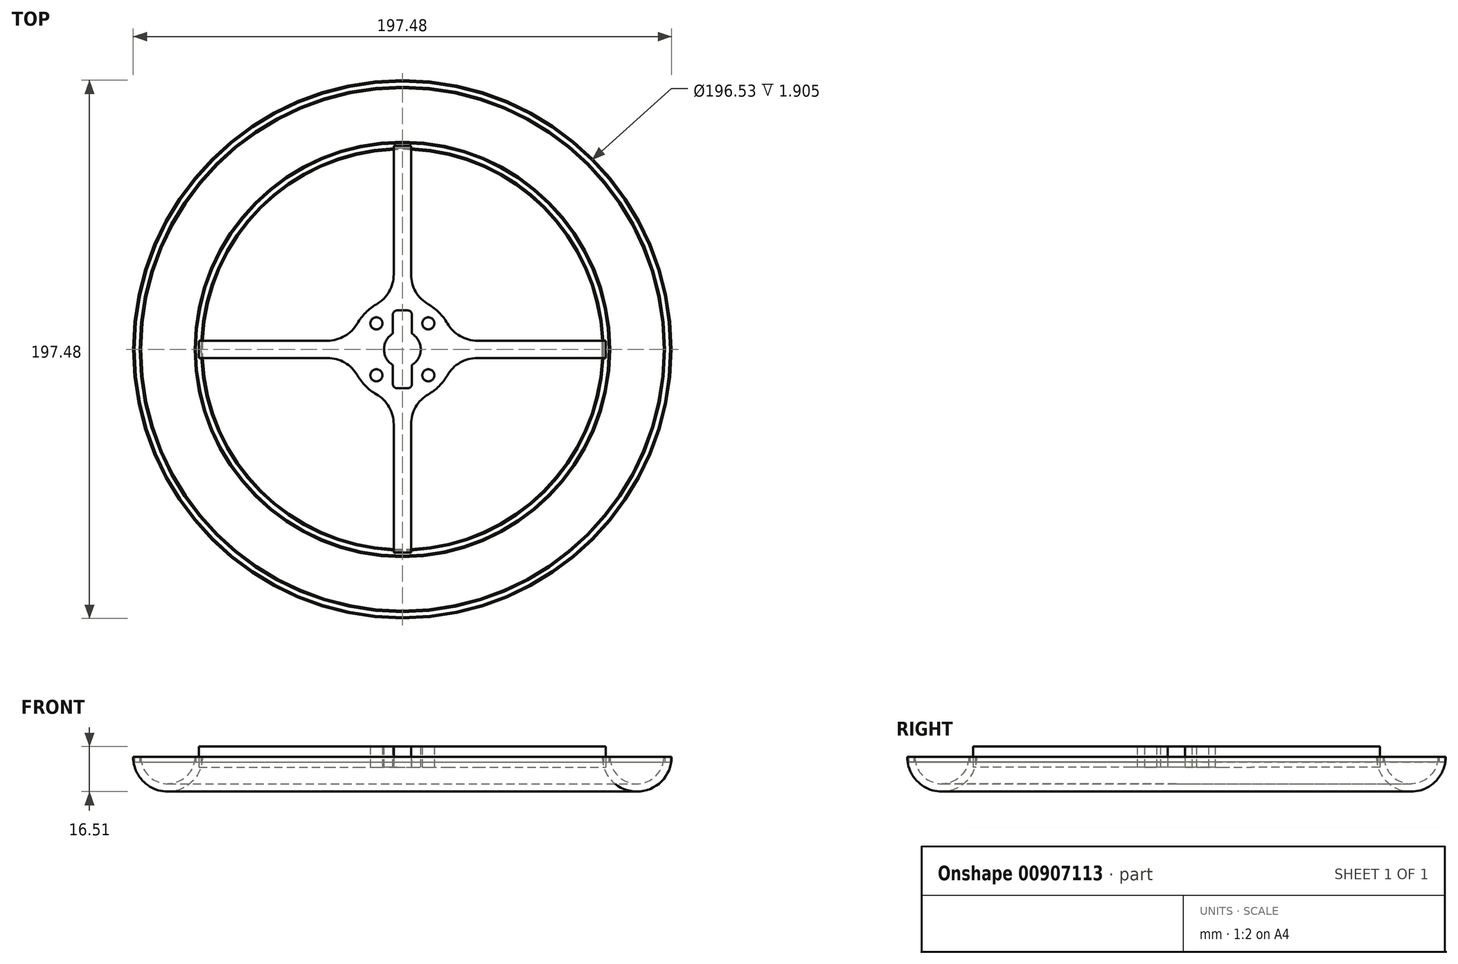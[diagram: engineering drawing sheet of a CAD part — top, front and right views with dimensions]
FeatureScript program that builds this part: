
annotation { "Feature Type Name" : "Feature", "Feature Type Description" : "" }
export const myFeature = defineFeature(function(context is Context, id is Id, definition is map)
    precondition{}
    {
        {
            var Q0;
            Q0=qCreatedBy(makeId("Front.planeOp"),FACE);
            var sketch = newSketch(context, id + "F0", { "sketchPlane" : qUnion([Q0])});
            skLineSegment(sketch, "E0", {"start": v(0, 25.4) * mm, "end": v(0, -25.4) * mm, "construction": true});
            skArc(sketch, "E1", {"start": v(-95.89, 0) * mm, "mid": v(-86.04, -9.84) * mm, "end": v(-76.2, 0) * mm});
            skArc(sketch, "E2", {"start": v(-98.74, 0) * mm, "mid": v(-86.04, -12.7) * mm, "end": v(-73.34, 0) * mm});
            skLineSegment(sketch, "E3", {"start": v(-98.74, 0) * mm, "end": v(-95.89, 0) * mm});
            skLineSegment(sketch, "E4.trimOffspring", {"start": v(-76.2, 0) * mm, "end": v(-73.34, 0) * mm});
            skSolve(sketch);
        }
        {
            var Q0;
            Q0=makeQuery(id+"F0.imprint","IMPRINT",FACE,{"disambiguationData":[TD([[makeQuery(id+"F0.imprint","IMPRINT",EDGE,{"derivedFrom":sQuery(id+"F0.wireOp",EDGE,"E1")}),1.0]])]});
            var Q1;
            Q1=makeQuery(id+"F0.imprint","IMPRINT",FACE,{"disambiguationData":[TD([[makeQuery(id+"F0.imprint","IMPRINT",EDGE,{"derivedFrom":sQuery(id+"F0.wireOp",EDGE,"E1")}),-1.0]])]});
            var Q2;
            Q2=sQuery(id+"F0.wireOp",EDGE,"E0");
            revolve(context, id + "F1", {"surfaceOperationType" : NewSurfaceOperationType.NEW, "entities" : qUnion([Q0, Q1]), "axis" : qUnion([Q2]), "revolveType" : RevolveType.FULL});
        }
        {
            var Q0;
            Q0=qCreatedBy(makeId("Front.planeOp"),FACE);
            var sketch = newSketch(context, id + "F2", { "sketchPlane" : qUnion([Q0])});
            skLineSegment(sketch, "E5.bottom", {"start": v(-98.27, 0) * mm, "end": v(-96.36, 0) * mm});
            skLineSegment(sketch, "E5.top", {"start": v(-98.27, -1.9) * mm, "end": v(-96.36, -1.9) * mm});
            skLineSegment(sketch, "E5.left", {"start": v(-98.27, 0) * mm, "end": v(-98.27, -1.9) * mm});
            skLineSegment(sketch, "E5.right", {"start": v(-96.36, 0) * mm, "end": v(-96.36, -1.9) * mm});
            skLineSegment(sketch, "E6.bottom", {"start": v(-75.72, 0) * mm, "end": v(-73.82, 0) * mm});
            skLineSegment(sketch, "E6.top", {"start": v(-75.72, -1.9) * mm, "end": v(-73.82, -1.9) * mm});
            skLineSegment(sketch, "E6.left", {"start": v(-75.72, 0) * mm, "end": v(-75.72, -1.9) * mm});
            skLineSegment(sketch, "E6.right", {"start": v(-73.82, 0) * mm, "end": v(-73.82, -1.9) * mm});
            skLineSegment(sketch, "E7", {"start": v(-97.31, 0) * mm, "end": v(-97.31, -1.9) * mm, "construction": true});
            skLineSegment(sketch, "E8", {"start": v(-98.27, -0.95) * mm, "end": v(-96.36, -0.95) * mm, "construction": true});
            skLineSegment(sketch, "E9", {"start": v(-74.77, 0) * mm, "end": v(-74.77, -1.9) * mm, "construction": true});
            skLineSegment(sketch, "E10", {"start": v(-75.72, -0.95) * mm, "end": v(-73.82, -0.95) * mm, "construction": true});
            skSolve(sketch);
        }
        {
            var Q0;
            Q0 = qSketchRegion(id + "F2", true);
            var Q1;
            Q1=sQuery(id+"F0.wireOp",EDGE,"E0");
            revolve(context, id + "F3", {"operationType" : NewBodyOperationType.REMOVE, "surfaceOperationType" : NewSurfaceOperationType.NEW, "entities" : qUnion([Q0]), "axis" : qUnion([Q1]), "revolveType" : RevolveType.FULL, "oppositeDirection" : true});
        }
        {
            var Q0;
            Q0=makeQuery(id+"F3.boolean.opBoolean","SPLIT",FACE,{"disambiguationData":[TD([makeQuery(id+"F1.opRevolve","SWEPT_FACE",FACE,{"disambiguationData":[OSD([sQuery(id+"F0.wireOp",EDGE,"E2")])]})])],"derivedFrom":makeQuery(id+"F1.opRevolve","SWEPT_FACE",FACE,{"disambiguationData":[OSD([sQuery(id+"F0.wireOp",EDGE,"E4.trimOffspring")])]})});
            var sketch = newSketch(context, id + "F4", { "sketchPlane" : qUnion([Q0])});
            skLineSegment(sketch, "E11.bottom", {"start": v(-50.8, 3.18) * mm, "end": v(50.8, 3.18) * mm});
            skLineSegment(sketch, "E11.top", {"start": v(-50.8, -3.17) * mm, "end": v(50.8, -3.17) * mm});
            skLineSegment(sketch, "E11.left", {"start": v(-50.8, 3.17) * mm, "end": v(-50.8, -3.17) * mm});
            skLineSegment(sketch, "E11.right", {"start": v(50.8, 3.17) * mm, "end": v(50.8, -3.17) * mm});
            skLineSegment(sketch, "E12.bottom", {"start": v(3.17, 50.8) * mm, "end": v(-3.17, 50.8) * mm});
            skLineSegment(sketch, "E12.top", {"start": v(3.17, -50.8) * mm, "end": v(-3.17, -50.8) * mm});
            skLineSegment(sketch, "E12.left", {"start": v(3.18, 50.8) * mm, "end": v(3.18, -50.8) * mm});
            skLineSegment(sketch, "E12.right", {"start": v(-3.17, 50.8) * mm, "end": v(-3.17, -50.8) * mm});
            skLineSegment(sketch, "E13", {"start": v(0, 50.8) * mm, "end": v(0, -50.8) * mm, "construction": true});
            skLineSegment(sketch, "E14", {"start": v(-3.18, 0) * mm, "end": v(3.17, 0) * mm, "construction": true});
            skLineSegment(sketch, "E15", {"start": v(-50.8, 0) * mm, "end": v(50.8, 0) * mm, "construction": true});
            skLineSegment(sketch, "E16", {"start": v(0, 3.17) * mm, "end": v(0, -3.17) * mm, "construction": true});
            skSolve(sketch);
        }
        {
            var Q0;
            {var subQ0=sQuery(id+"F4.wireOp",EDGE,"E11.left");Q0=makeQuery(id+"F4.imprint","IMPRINT",FACE,{"disambiguationData":[TD([[makeQuery(id+"F4.imprint","IMPRINT",EDGE,{"derivedFrom":subQ0}),1.0]])]});}
            var Q1;
            {var subQ0=sQuery(id+"F4.wireOp",EDGE,"E11.right");Q1=makeQuery(id+"F4.imprint","IMPRINT",FACE,{"disambiguationData":[TD([[makeQuery(id+"F4.imprint","IMPRINT",EDGE,{"derivedFrom":subQ0}),-1.0]])]});}
            var Q2;
            {var subQ5=sQuery(id+"F4.wireOp",EDGE,"E12.bottom");Q2=makeQuery(id+"F4.imprint","IMPRINT",FACE,{"disambiguationData":[TD([[makeQuery(id+"F4.imprint","IMPRINT",EDGE,{"derivedFrom":subQ5}),1.0]])]});}
            var Q3;
            {var subQ5=sQuery(id+"F4.wireOp",EDGE,"E12.top");Q3=makeQuery(id+"F4.imprint","IMPRINT",FACE,{"disambiguationData":[TD([[makeQuery(id+"F4.imprint","IMPRINT",EDGE,{"derivedFrom":subQ5}),-1.0]])]});}
            var Q4;
            {var subQ0=sQuery(id+"F4.wireOp",EDGE,"E12.right");var subQ1=sQuery(id+"F4.wireOp",EDGE,"E11.bottom");var subQ2=makeQuery(id+"F4.imprint","INTERSECT",VERTEX,{"derivedFrom":[subQ1,subQ0]});Q4=makeQuery(id+"F4.imprint","IMPRINT",FACE,{"disambiguationData":[TD([[makeQuery(id+"F4.imprint","IMPRINT",EDGE,{"disambiguationData":[TD([[subQ2,-1.0]])],"derivedFrom":subQ1}),-1.0]])]});}
            extrude(context, id + "F5", {"entities" : qUnion([Q0, Q1, Q2, Q3, Q4]), "depth" : 25.4 * mm, "offsetDistance" : 25.4 * mm});
        }
        {
            var Q0;
            Q0=makeQuery(id+"F5.opExtrude","SWEPT_BODY",BODY,{"disambiguationData":[OSD([sQuery(id+"F4.wireOp",EDGE,"E11.bottom"),sQuery(id+"F4.wireOp",EDGE,"E11.top"),sQuery(id+"F4.wireOp",EDGE,"E11.left"),sQuery(id+"F4.wireOp",EDGE,"E11.right"),sQuery(id+"F4.wireOp",EDGE,"E12.bottom"),sQuery(id+"F4.wireOp",EDGE,"E12.top"),sQuery(id+"F4.wireOp",EDGE,"E12.left"),sQuery(id+"F4.wireOp",EDGE,"E12.right")])]});
            deleteBodies(context, id + "F6", {"entities" : qUnion([Q0])});
        }
        {
            var Q0;
            Q0=qCreatedBy(makeId("Top.planeOp"),FACE);
            var sketch = newSketch(context, id + "F7", { "sketchPlane" : qUnion([Q0])});
            skLineSegment(sketch, "E17.bottom", {"start": v(-74.61, 3.17) * mm, "end": v(74.61, 3.17) * mm});
            skLineSegment(sketch, "E17.top", {"start": v(-74.61, -3.18) * mm, "end": v(74.61, -3.18) * mm});
            skLineSegment(sketch, "E17.left", {"start": v(74.61, 3.18) * mm, "end": v(74.61, -3.17) * mm});
            skLineSegment(sketch, "E17.right", {"start": v(-74.61, 3.18) * mm, "end": v(-74.61, -3.18) * mm});
            skLineSegment(sketch, "E18", {"start": v(74.61, 0) * mm, "end": v(-74.61, 0) * mm, "construction": true});
            skLineSegment(sketch, "E19", {"start": v(0, 3.17) * mm, "end": v(0, -3.17) * mm, "construction": true});
            skLineSegment(sketch, "E20.bottom", {"start": v(-3.18, 74.61) * mm, "end": v(3.18, 74.61) * mm});
            skLineSegment(sketch, "E20.top", {"start": v(-3.18, -74.61) * mm, "end": v(3.18, -74.61) * mm});
            skLineSegment(sketch, "E20.left", {"start": v(-3.18, 74.61) * mm, "end": v(-3.18, -74.61) * mm});
            skLineSegment(sketch, "E20.right", {"start": v(3.17, 74.61) * mm, "end": v(3.17, -74.61) * mm});
            skLineSegment(sketch, "E21", {"start": v(0, 74.61) * mm, "end": v(0, -74.61) * mm, "construction": true});
            skLineSegment(sketch, "E22", {"start": v(-3.17, 0) * mm, "end": v(3.17, 0) * mm, "construction": true});
            skCircle(sketch, "E23", {"center": v(0, 0) * mm, "radius": 19.05 * mm});
            skSolve(sketch);
        }
        {
            var Q0;
            {var subQ0=sQuery(id+"F7.wireOp",EDGE,"E17.right");Q0=makeQuery(id+"F7.imprint","IMPRINT",FACE,{"disambiguationData":[TD([[makeQuery(id+"F7.imprint","IMPRINT",EDGE,{"derivedFrom":subQ0}),1.0]])]});}
            var Q1;
            {var subQ0=sQuery(id+"F7.wireOp",EDGE,"E17.left");Q1=makeQuery(id+"F7.imprint","IMPRINT",FACE,{"disambiguationData":[TD([[makeQuery(id+"F7.imprint","IMPRINT",EDGE,{"derivedFrom":subQ0}),-1.0]])]});}
            var Q2;
            {var subQ5=sQuery(id+"F7.wireOp",EDGE,"E20.bottom");Q2=makeQuery(id+"F7.imprint","IMPRINT",FACE,{"disambiguationData":[TD([[makeQuery(id+"F7.imprint","IMPRINT",EDGE,{"derivedFrom":subQ5}),-1.0]])]});}
            var Q3;
            {var subQ5=sQuery(id+"F7.wireOp",EDGE,"E20.top");Q3=makeQuery(id+"F7.imprint","IMPRINT",FACE,{"disambiguationData":[TD([[makeQuery(id+"F7.imprint","IMPRINT",EDGE,{"derivedFrom":subQ5}),1.0]])]});}
            var Q4;
            {var subQ0=sQuery(id+"F7.wireOp",EDGE,"E20.left");var subQ1=sQuery(id+"F7.wireOp",EDGE,"E17.bottom");var subQ2=makeQuery(id+"F7.imprint","INTERSECT",VERTEX,{"derivedFrom":[subQ1,subQ0]});Q4=makeQuery(id+"F7.imprint","IMPRINT",FACE,{"disambiguationData":[TD([[makeQuery(id+"F7.imprint","IMPRINT",EDGE,{"disambiguationData":[TD([[subQ2,-1.0]])],"derivedFrom":subQ1}),-1.0]])]});}
            var Q5;
            {var subQ0=sQuery(id+"F7.wireOp",EDGE,"E23");var subQ1=sQuery(id+"F7.wireOp",EDGE,"E17.bottom");var subQ2=makeQuery(id+"F7.imprint","INTERSECT",VERTEX,{"disambiguationData":[OD(0.0)],"derivedFrom":[subQ1,subQ0]});Q5=makeQuery(id+"F7.imprint","IMPRINT",FACE,{"disambiguationData":[TD([[makeQuery(id+"F7.imprint","IMPRINT",EDGE,{"disambiguationData":[TD([[subQ2,-1.0]])],"derivedFrom":subQ1}),-1.0]])]});}
            var Q6;
            {var subQ0=sQuery(id+"F7.wireOp",EDGE,"E23");var subQ1=sQuery(id+"F7.wireOp",EDGE,"E17.bottom");var subQ2=makeQuery(id+"F7.imprint","INTERSECT",VERTEX,{"disambiguationData":[OD(1.0)],"derivedFrom":[subQ1,subQ0]});Q6=makeQuery(id+"F7.imprint","IMPRINT",FACE,{"disambiguationData":[TD([[makeQuery(id+"F7.imprint","IMPRINT",EDGE,{"disambiguationData":[TD([[subQ2,1.0]])],"derivedFrom":subQ1}),-1.0]])]});}
            var Q7;
            {var subQ0=sQuery(id+"F7.wireOp",EDGE,"E20.left");var subQ1=sQuery(id+"F7.wireOp",EDGE,"E17.top");var subQ2=makeQuery(id+"F7.imprint","INTERSECT",VERTEX,{"derivedFrom":[subQ1,subQ0]});Q7=makeQuery(id+"F7.imprint","IMPRINT",FACE,{"disambiguationData":[TD([[makeQuery(id+"F7.imprint","IMPRINT",EDGE,{"disambiguationData":[TD([[subQ2,-1.0]])],"derivedFrom":subQ1}),-1.0]])]});}
            var Q8;
            {var subQ0=sQuery(id+"F7.wireOp",EDGE,"E20.left");var subQ1=sQuery(id+"F7.wireOp",EDGE,"E17.bottom");var subQ2=makeQuery(id+"F7.imprint","INTERSECT",VERTEX,{"derivedFrom":[subQ1,subQ0]});Q8=makeQuery(id+"F7.imprint","IMPRINT",FACE,{"disambiguationData":[TD([[makeQuery(id+"F7.imprint","IMPRINT",EDGE,{"disambiguationData":[TD([[subQ2,-1.0]])],"derivedFrom":subQ1}),1.0]])]});}
            var Q9;
            {var subQ0=sQuery(id+"F7.wireOp",EDGE,"E23");var subQ1=sQuery(id+"F7.wireOp",EDGE,"E17.bottom");var subQ2=makeQuery(id+"F7.imprint","INTERSECT",VERTEX,{"disambiguationData":[OD(1.0)],"derivedFrom":[subQ1,subQ0]});Q9=makeQuery(id+"F7.imprint","IMPRINT",FACE,{"disambiguationData":[TD([[makeQuery(id+"F7.imprint","IMPRINT",EDGE,{"disambiguationData":[TD([[subQ2,1.0]])],"derivedFrom":subQ1}),1.0]])]});}
            var Q10;
            {var subQ0=sQuery(id+"F7.wireOp",EDGE,"E23");var subQ1=sQuery(id+"F7.wireOp",EDGE,"E17.bottom");var subQ2=makeQuery(id+"F7.imprint","INTERSECT",VERTEX,{"disambiguationData":[OD(0.0)],"derivedFrom":[subQ1,subQ0]});Q10=makeQuery(id+"F7.imprint","IMPRINT",FACE,{"disambiguationData":[TD([[makeQuery(id+"F7.imprint","IMPRINT",EDGE,{"disambiguationData":[TD([[subQ2,-1.0]])],"derivedFrom":subQ1}),1.0]])]});}
            var Q11;
            {var subQ0=sQuery(id+"F7.wireOp",EDGE,"E23");var subQ1=sQuery(id+"F7.wireOp",EDGE,"E17.top");var subQ2=makeQuery(id+"F7.imprint","INTERSECT",VERTEX,{"disambiguationData":[OD(0.0)],"derivedFrom":[subQ1,subQ0]});Q11=makeQuery(id+"F7.imprint","IMPRINT",FACE,{"disambiguationData":[TD([[makeQuery(id+"F7.imprint","IMPRINT",EDGE,{"disambiguationData":[TD([[subQ2,-1.0]])],"derivedFrom":subQ1}),-1.0]])]});}
            var Q12;
            {var subQ0=sQuery(id+"F7.wireOp",EDGE,"E23");var subQ1=sQuery(id+"F7.wireOp",EDGE,"E17.top");var subQ2=makeQuery(id+"F7.imprint","INTERSECT",VERTEX,{"disambiguationData":[OD(1.0)],"derivedFrom":[subQ1,subQ0]});Q12=makeQuery(id+"F7.imprint","IMPRINT",FACE,{"disambiguationData":[TD([[makeQuery(id+"F7.imprint","IMPRINT",EDGE,{"disambiguationData":[TD([[subQ2,1.0]])],"derivedFrom":subQ1}),-1.0]])]});}
            extrude(context, id + "F8", {"entities" : qUnion([Q0, Q1, Q2, Q3, Q4, Q5, Q6, Q7, Q8, Q9, Q10, Q11, Q12]), "depth" : 3.8 * mm, "offsetDistance" : 25.4 * mm, "hasSecondDirection" : true, "secondDirectionOppositeDirection" : true, "secondDirectionDepth" : 3.8 * mm});
        }
        {
            var Q0;
            {var subQ0=sQuery(id+"F7.wireOp",EDGE,"E23");var subQ1=sQuery(id+"F7.wireOp",EDGE,"E20.right");Q0=makeQuery(id+"F8.opExtrude","SWEPT_EDGE",EDGE,{"disambiguationData":[OSD([subQ1,subQ0]),TDD([makeQuery(id+"F7.imprint","INTERSECT",VERTEX,{"disambiguationData":[OD(1.0)],"derivedFrom":[subQ1,subQ0]})])]});}
            var Q1;
            {var subQ0=sQuery(id+"F7.wireOp",EDGE,"E23");var subQ1=sQuery(id+"F7.wireOp",EDGE,"E17.top");Q1=makeQuery(id+"F8.opExtrude","SWEPT_EDGE",EDGE,{"disambiguationData":[OSD([subQ1,subQ0]),TDD([makeQuery(id+"F7.imprint","INTERSECT",VERTEX,{"disambiguationData":[OD(1.0)],"derivedFrom":[subQ1,subQ0]})])]});}
            var Q2;
            {var subQ0=sQuery(id+"F7.wireOp",EDGE,"E23");var subQ1=sQuery(id+"F7.wireOp",EDGE,"E20.left");Q2=makeQuery(id+"F8.opExtrude","SWEPT_EDGE",EDGE,{"disambiguationData":[OSD([subQ1,subQ0]),TDD([makeQuery(id+"F7.imprint","INTERSECT",VERTEX,{"disambiguationData":[OD(1.0)],"derivedFrom":[subQ1,subQ0]})])]});}
            var Q3;
            {var subQ0=sQuery(id+"F7.wireOp",EDGE,"E23");var subQ1=sQuery(id+"F7.wireOp",EDGE,"E17.top");Q3=makeQuery(id+"F8.opExtrude","SWEPT_EDGE",EDGE,{"disambiguationData":[OSD([subQ1,subQ0]),TDD([makeQuery(id+"F7.imprint","INTERSECT",VERTEX,{"disambiguationData":[OD(0.0)],"derivedFrom":[subQ1,subQ0]})])]});}
            var Q4;
            {var subQ0=sQuery(id+"F7.wireOp",EDGE,"E23");var subQ1=sQuery(id+"F7.wireOp",EDGE,"E17.bottom");Q4=makeQuery(id+"F8.opExtrude","SWEPT_EDGE",EDGE,{"disambiguationData":[OSD([subQ1,subQ0]),TDD([makeQuery(id+"F7.imprint","INTERSECT",VERTEX,{"disambiguationData":[OD(0.0)],"derivedFrom":[subQ1,subQ0]})])]});}
            var Q5;
            {var subQ0=sQuery(id+"F7.wireOp",EDGE,"E23");var subQ1=sQuery(id+"F7.wireOp",EDGE,"E20.left");Q5=makeQuery(id+"F8.opExtrude","SWEPT_EDGE",EDGE,{"disambiguationData":[OSD([subQ1,subQ0]),TDD([makeQuery(id+"F7.imprint","INTERSECT",VERTEX,{"disambiguationData":[OD(0.0)],"derivedFrom":[subQ1,subQ0]})])]});}
            var Q6;
            {var subQ0=sQuery(id+"F7.wireOp",EDGE,"E23");var subQ1=sQuery(id+"F7.wireOp",EDGE,"E20.right");Q6=makeQuery(id+"F8.opExtrude","SWEPT_EDGE",EDGE,{"disambiguationData":[OSD([subQ1,subQ0]),TDD([makeQuery(id+"F7.imprint","INTERSECT",VERTEX,{"disambiguationData":[OD(0.0)],"derivedFrom":[subQ1,subQ0]})])]});}
            var Q7;
            {var subQ0=sQuery(id+"F7.wireOp",EDGE,"E23");var subQ1=sQuery(id+"F7.wireOp",EDGE,"E17.bottom");Q7=makeQuery(id+"F8.opExtrude","SWEPT_EDGE",EDGE,{"disambiguationData":[OSD([subQ1,subQ0]),TDD([makeQuery(id+"F7.imprint","INTERSECT",VERTEX,{"disambiguationData":[OD(1.0)],"derivedFrom":[subQ1,subQ0]})])]});}
            fillet(context, id + "F9", {"entities" : qUnion([Q0, Q1, Q2, Q3, Q4, Q5, Q6, Q7]), "radius" : 12.7 * mm, "tangentPropagation" : true, "allowEdgeOverflow" : false});
        }
        {
            var Q0;
            Q0=makeQuery(id+"F8.opExtrude","CAP_FACE",FACE,{"disambiguationData":[OSD([sQuery(id+"F7.wireOp",EDGE,"E17.bottom"),sQuery(id+"F7.wireOp",EDGE,"E17.top"),sQuery(id+"F7.wireOp",EDGE,"E17.left"),sQuery(id+"F7.wireOp",EDGE,"E17.right"),sQuery(id+"F7.wireOp",EDGE,"E20.bottom"),sQuery(id+"F7.wireOp",EDGE,"E20.top"),sQuery(id+"F7.wireOp",EDGE,"E20.left"),sQuery(id+"F7.wireOp",EDGE,"E20.right"),sQuery(id+"F7.wireOp",EDGE,"E23")])],"isStart":false});
            var sketch = newSketch(context, id + "F10", { "sketchPlane" : qUnion([Q0])});
            skCircle(sketch, "E24", {"center": v(0, 0) * mm, "radius": 6.75 * mm});
            skLineSegment(sketch, "E25.bottom", {"start": v(-3.5, 14.29) * mm, "end": v(3.5, 14.29) * mm});
            skLineSegment(sketch, "E25.top", {"start": v(-3.5, -14.29) * mm, "end": v(3.5, -14.29) * mm});
            skLineSegment(sketch, "E25.left", {"start": v(-3.5, 14.29) * mm, "end": v(-3.5, -14.29) * mm});
            skLineSegment(sketch, "E25.right", {"start": v(3.5, 14.29) * mm, "end": v(3.5, -14.29) * mm});
            skLineSegment(sketch, "E26", {"start": v(0, 14.29) * mm, "end": v(0, -14.29) * mm, "construction": true});
            skLineSegment(sketch, "E27", {"start": v(-3.5, 0) * mm, "end": v(3.5, 0) * mm, "construction": true});
            skSolve(sketch);
        }
        {
            var Q0;
            {var subQ0=sQuery(id+"F10.wireOp",EDGE,"E25.left");var subQ1=sQuery(id+"F10.wireOp",EDGE,"E24");var subQ2=makeQuery(id+"F10.imprint","INTERSECT",VERTEX,{"disambiguationData":[OD(0.0)],"derivedFrom":[subQ1,subQ0]});Q0=makeQuery(id+"F10.imprint","IMPRINT",FACE,{"disambiguationData":[TD([[makeQuery(id+"F10.imprint","IMPRINT",EDGE,{"disambiguationData":[TD([[subQ2,-1.0]])],"derivedFrom":subQ1}),1.0]])]});}
            var Q1;
            {var subQ0=sQuery(id+"F10.wireOp",EDGE,"E25.right");var subQ1=sQuery(id+"F10.wireOp",EDGE,"E24");var subQ2=makeQuery(id+"F10.imprint","INTERSECT",VERTEX,{"disambiguationData":[OD(0.0)],"derivedFrom":[subQ1,subQ0]});Q1=makeQuery(id+"F10.imprint","IMPRINT",FACE,{"disambiguationData":[TD([[makeQuery(id+"F10.imprint","IMPRINT",EDGE,{"disambiguationData":[TD([[subQ2,1.0]])],"derivedFrom":subQ1}),1.0]])]});}
            var Q2;
            {var subQ5=sQuery(id+"F10.wireOp",EDGE,"E25.bottom");Q2=makeQuery(id+"F10.imprint","IMPRINT",FACE,{"disambiguationData":[TD([[makeQuery(id+"F10.imprint","IMPRINT",EDGE,{"derivedFrom":subQ5}),-1.0]])]});}
            var Q3;
            {var subQ5=sQuery(id+"F10.wireOp",EDGE,"E25.top");Q3=makeQuery(id+"F10.imprint","IMPRINT",FACE,{"disambiguationData":[TD([[makeQuery(id+"F10.imprint","IMPRINT",EDGE,{"derivedFrom":subQ5}),1.0]])]});}
            var Q4;
            {var subQ0=sQuery(id+"F10.wireOp",EDGE,"E25.left");var subQ1=sQuery(id+"F10.wireOp",EDGE,"E24");var subQ2=makeQuery(id+"F10.imprint","INTERSECT",VERTEX,{"disambiguationData":[OD(0.0)],"derivedFrom":[subQ1,subQ0]});Q4=makeQuery(id+"F10.imprint","IMPRINT",FACE,{"disambiguationData":[TD([[makeQuery(id+"F10.imprint","IMPRINT",EDGE,{"disambiguationData":[TD([[subQ2,1.0]])],"derivedFrom":subQ1}),1.0]])]});}
            extrude(context, id + "F11", {"entities" : qUnion([Q0, Q1, Q2, Q3, Q4]), "operationType" : NewBodyOperationType.REMOVE, "oppositeDirection" : true, "depth" : 25.4 * mm, "offsetDistance" : 25.4 * mm});
        }
        {
            var Q0;
            Q0=makeQuery(id+"F11.boolean.opBoolean","COPY",EDGE,{"derivedFrom":makeQuery(id+"F11.opExtrude","SWEPT_EDGE",EDGE,{"disambiguationData":[OSD([sQuery(id+"F10.wireOp",EDGE,"E25.bottom"),sQuery(id+"F10.wireOp",EDGE,"E25.right")])]})});
            var Q1;
            Q1=makeQuery(id+"F11.boolean.opBoolean","COPY",EDGE,{"derivedFrom":makeQuery(id+"F11.opExtrude","SWEPT_EDGE",EDGE,{"disambiguationData":[OSD([sQuery(id+"F10.wireOp",EDGE,"E25.top"),sQuery(id+"F10.wireOp",EDGE,"E25.right")])]})});
            var Q2;
            Q2=makeQuery(id+"F11.boolean.opBoolean","COPY",EDGE,{"derivedFrom":makeQuery(id+"F11.opExtrude","SWEPT_EDGE",EDGE,{"disambiguationData":[OSD([sQuery(id+"F10.wireOp",EDGE,"E25.bottom"),sQuery(id+"F10.wireOp",EDGE,"E25.left")])]})});
            var Q3;
            Q3=makeQuery(id+"F11.boolean.opBoolean","COPY",EDGE,{"derivedFrom":makeQuery(id+"F11.opExtrude","SWEPT_EDGE",EDGE,{"disambiguationData":[OSD([sQuery(id+"F10.wireOp",EDGE,"E25.top"),sQuery(id+"F10.wireOp",EDGE,"E25.left")])]})});
            fillet(context, id + "F12", {"entities" : qUnion([Q0, Q1, Q2, Q3]), "radius" : 1.59 * mm, "tangentPropagation" : true, "allowEdgeOverflow" : false});
        }
        {
            var Q0;
            Q0=makeQuery(id+"F8.opExtrude","CAP_FACE",FACE,{"disambiguationData":[OSD([sQuery(id+"F7.wireOp",EDGE,"E17.bottom"),sQuery(id+"F7.wireOp",EDGE,"E17.top"),sQuery(id+"F7.wireOp",EDGE,"E17.left"),sQuery(id+"F7.wireOp",EDGE,"E17.right"),sQuery(id+"F7.wireOp",EDGE,"E20.bottom"),sQuery(id+"F7.wireOp",EDGE,"E20.top"),sQuery(id+"F7.wireOp",EDGE,"E20.left"),sQuery(id+"F7.wireOp",EDGE,"E20.right"),sQuery(id+"F7.wireOp",EDGE,"E23")])],"isStart":true});
            var sketch = newSketch(context, id + "F13", { "sketchPlane" : qUnion([Q0])});
            skCircle(sketch, "E28", {"center": v(-9.52, 9.52) * mm, "radius": 2.22 * mm});
            skCircle(sketch, "E29", {"center": v(9.53, 9.53) * mm, "radius": 2.22 * mm});
            skCircle(sketch, "E30", {"center": v(9.53, -9.53) * mm, "radius": 2.22 * mm});
            skCircle(sketch, "E31", {"center": v(-9.52, -9.53) * mm, "radius": 2.22 * mm});
            skSolve(sketch);
        }
        {
            var Q0;
            Q0=makeQuery(id+"F13.imprint","IMPRINT",FACE,{"disambiguationData":[TD([[makeQuery(id+"F13.imprint","IMPRINT",EDGE,{"derivedFrom":sQuery(id+"F13.wireOp",EDGE,"E28")}),1.0]])]});
            var Q1;
            Q1=makeQuery(id+"F13.imprint","IMPRINT",FACE,{"disambiguationData":[TD([[makeQuery(id+"F13.imprint","IMPRINT",EDGE,{"derivedFrom":sQuery(id+"F13.wireOp",EDGE,"E29")}),1.0]])]});
            var Q2;
            Q2=makeQuery(id+"F13.imprint","IMPRINT",FACE,{"disambiguationData":[TD([[makeQuery(id+"F13.imprint","IMPRINT",EDGE,{"derivedFrom":sQuery(id+"F13.wireOp",EDGE,"E30")}),1.0]])]});
            var Q3;
            Q3=makeQuery(id+"F13.imprint","IMPRINT",FACE,{"disambiguationData":[TD([[makeQuery(id+"F13.imprint","IMPRINT",EDGE,{"derivedFrom":sQuery(id+"F13.wireOp",EDGE,"E31")}),1.0]])]});
            extrude(context, id + "F14", {"entities" : qUnion([Q0, Q1, Q2, Q3]), "operationType" : NewBodyOperationType.REMOVE, "oppositeDirection" : true, "depth" : 25.4 * mm, "offsetDistance" : 25.4 * mm});
        }
    });
